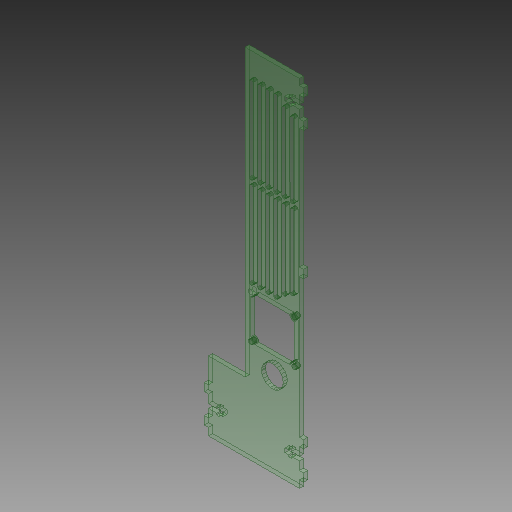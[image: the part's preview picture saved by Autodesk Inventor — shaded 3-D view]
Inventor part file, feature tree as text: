
AUTODESK INVENTOR PART (.ipt)
format: ipt  version: 2018 (Build 220112000, 112)  size: 729,600 bytes
history: native  units: mm
features: sketch x2, extrude x1, hole x1
ambient origin geometry x8: Origin, YZ Plane, XZ Plane, XY Plane, X Axis, Y Axis, Z Axis, Center Point
bodies: Solid1 (feature_tree)
feature tree (4):
  extrude  "Extrusion1"  [1 undecoded]
  hole  "Hole1"  [1 undecoded]
  sketch  "Sketch1"  dims[d0=3.0mm d1=0.0mm]
  sketch  "Sketch2"  dims[d2=3.4mm d3=6.0mm d4=4.0mm d5=2.0mm d6=90.0deg d7=8.0mm d8=20.594885mm]
note: 2 required parameter values undecoded (feature->parameter linkage not recoverable at this tier; creation-order binding heuristic only, values carry confidence <= 0.55)
